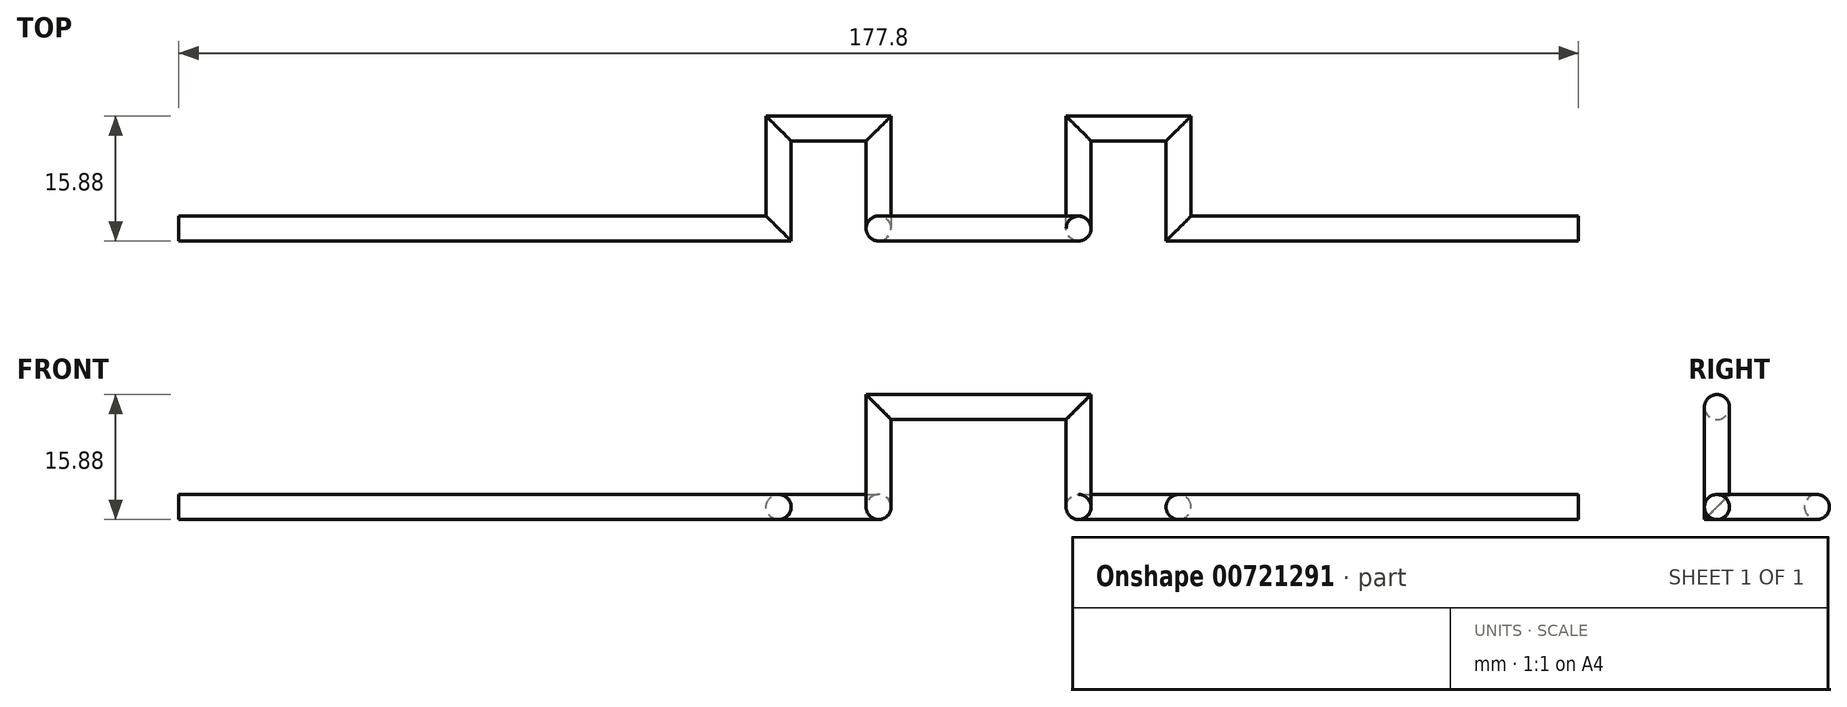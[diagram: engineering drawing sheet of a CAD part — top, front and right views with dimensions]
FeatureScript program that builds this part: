
annotation { "Feature Type Name" : "Feature", "Feature Type Description" : "" }
export const myFeature = defineFeature(function(context is Context, id is Id, definition is map)
    precondition{}
    {
        {
            var Q0;
            Q0=qCreatedBy(makeId("Top.planeOp"),FACE);
            var sketch = newSketch(context, id + "F0", { "sketchPlane" : qUnion([Q0])});
            skLineSegment(sketch, "E0", {"start": v(80.26, 0) * mm, "end": v(29.46, 0) * mm});
            skLineSegment(sketch, "E1", {"start": v(29.46, 0) * mm, "end": v(29.46, 12.7) * mm});
            skLineSegment(sketch, "E2", {"start": v(29.46, 12.7) * mm, "end": v(16.76, 12.7) * mm});
            skLineSegment(sketch, "E3", {"start": v(16.76, 12.7) * mm, "end": v(16.76, 0) * mm});
            skLineSegment(sketch, "E4", {"start": v(-8.64, 0) * mm, "end": v(-8.64, 12.7) * mm});
            skLineSegment(sketch, "E5", {"start": v(-8.64, 12.7) * mm, "end": v(-21.34, 12.7) * mm});
            skLineSegment(sketch, "E6", {"start": v(-21.34, 12.7) * mm, "end": v(-21.34, 0) * mm});
            skLineSegment(sketch, "E7", {"start": v(-21.34, 0) * mm, "end": v(-97.54, 0) * mm});
            skSolve(sketch);
        }
        {
            var Q0;
            Q0=qCreatedBy(makeId("Front.planeOp"),FACE);
            var sketch = newSketch(context, id + "F1", { "sketchPlane" : qUnion([Q0])});
            skLineSegment(sketch, "E8", {"start": v(-8.64, 0) * mm, "end": v(-8.64, 12.7) * mm});
            skLineSegment(sketch, "E9", {"start": v(-8.64, 12.7) * mm, "end": v(16.76, 12.7) * mm});
            skLineSegment(sketch, "E10", {"start": v(16.76, 12.7) * mm, "end": v(16.76, 0) * mm});
            skSolve(sketch);
        }
        {
            var Q0;
            Q0=qCreatedBy(makeId("Right.planeOp"),FACE);
            var sketch = newSketch(context, id + "F2", { "sketchPlane" : qUnion([Q0])});
            skCircle(sketch, "E11", {"center": v(0, 12.7) * mm, "radius": 1.59 * mm});
            skSolve(sketch);
        }
        {
            var Q0;
            Q0=makeQuery(id+"F2.imprint","IMPRINT",FACE,{"disambiguationData":[TD([[makeQuery(id+"F2.imprint","IMPRINT",EDGE,{"derivedFrom":sQuery(id+"F2.wireOp",EDGE,"E11")}),1.0]])]});
            var Q1;
            Q1=sQuery(id+"F1.wireOp",EDGE,"E9");
            var Q2;
            Q2=sQuery(id+"F1.wireOp",EDGE,"E10");
            var Q3;
            Q3=sQuery(id+"F1.wireOp",EDGE,"E8");
            var Q4;
            Q4=sQuery(id+"F0.wireOp",EDGE,"E3");
            var Q5;
            Q5=sQuery(id+"F0.wireOp",EDGE,"E2");
            var Q6;
            Q6=sQuery(id+"F0.wireOp",EDGE,"E0");
            var Q7;
            Q7=sQuery(id+"F0.wireOp",EDGE,"E1");
            var Q8;
            Q8=sQuery(id+"F0.wireOp",EDGE,"E4");
            var Q9;
            Q9=sQuery(id+"F0.wireOp",EDGE,"E5");
            var Q10;
            Q10=sQuery(id+"F0.wireOp",EDGE,"E6");
            var Q11;
            Q11=sQuery(id+"F0.wireOp",EDGE,"E7");
            sweep(context, id + "F3", {"profiles" : qUnion([Q0]), "path" : qUnion([Q1, Q2, Q3, Q4, Q5, Q6, Q7, Q8, Q9, Q10, Q11])});
        }
    });
